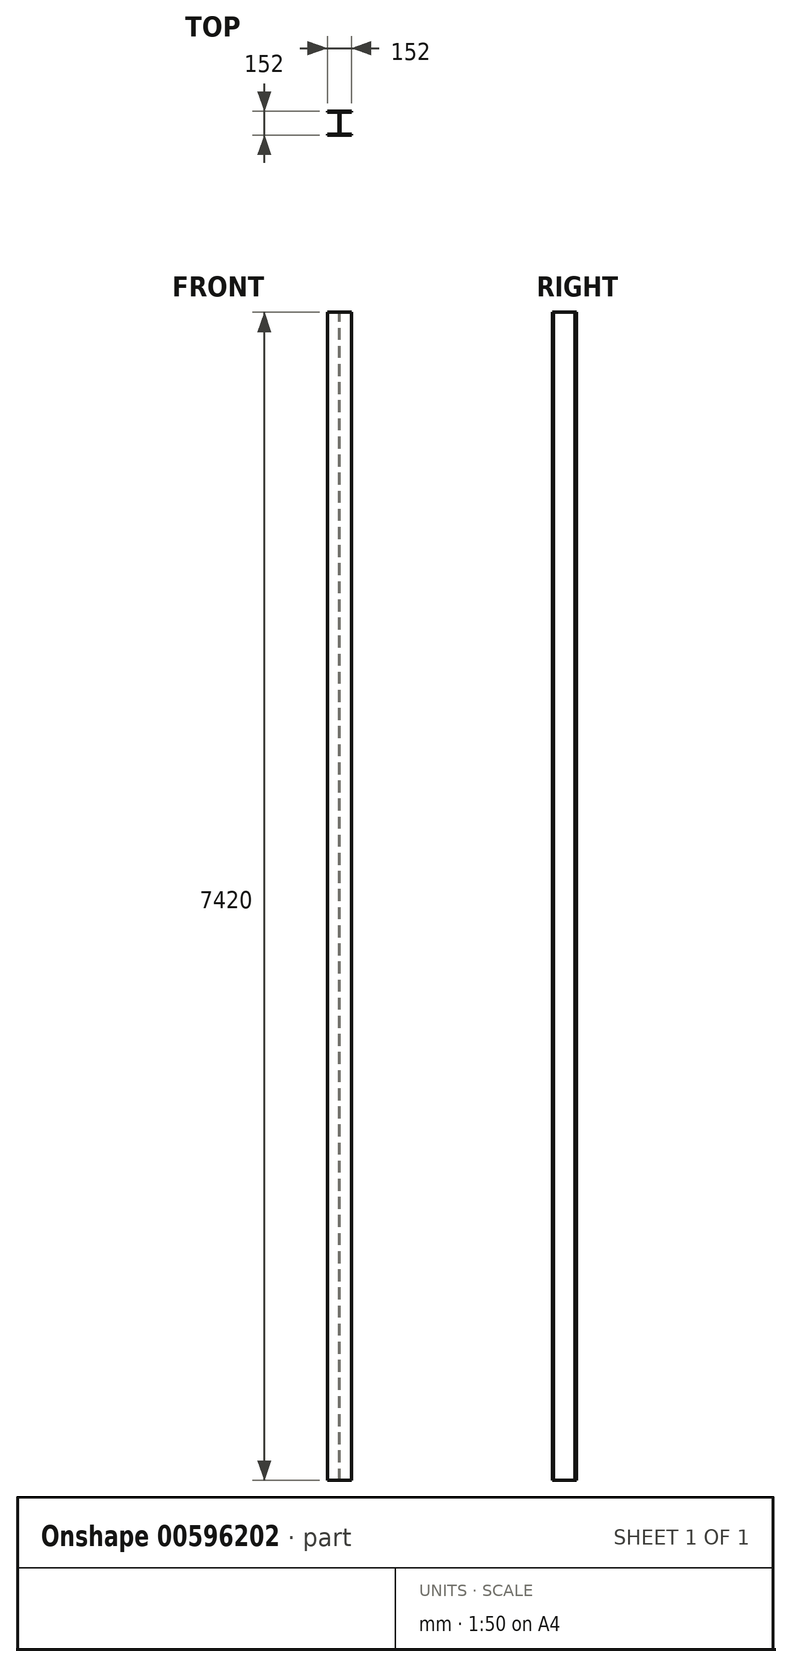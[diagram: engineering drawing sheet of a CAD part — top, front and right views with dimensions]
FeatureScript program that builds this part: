
annotation { "Feature Type Name" : "Feature", "Feature Type Description" : "" }
export const myFeature = defineFeature(function(context is Context, id is Id, definition is map)
    precondition{}
    {
        {
            var Q0;
            Q0=qCreatedBy(makeId("Top.planeOp"),FACE);
            var sketch = newSketch(context, id + "F0", { "sketchPlane" : qUnion([Q0])});
            skLineSegment(sketch, "E0.bottom", {"start": v(-132.33, 137.4) * mm, "end": v(19.67, 137.4) * mm, "construction": true});
            skLineSegment(sketch, "E0.top", {"start": v(-132.33, -14.6) * mm, "end": v(19.67, -14.6) * mm, "construction": true});
            skLineSegment(sketch, "E0.left", {"start": v(-132.33, 137.4) * mm, "end": v(-132.33, -14.6) * mm, "construction": true});
            skLineSegment(sketch, "E0.right", {"start": v(19.67, 137.4) * mm, "end": v(19.67, -14.6) * mm, "construction": true});
            skLineSegment(sketch, "E1", {"start": v(-59.38, 137.4) * mm, "end": v(-59.38, -14.6) * mm, "construction": true});
            skLineSegment(sketch, "E2", {"start": v(-53.28, 137.4) * mm, "end": v(-53.28, -14.6) * mm, "construction": true});
            skLineSegment(sketch, "E3", {"start": v(-132.33, 130.6) * mm, "end": v(19.67, 130.6) * mm, "construction": true});
            skLineSegment(sketch, "E4", {"start": v(-132.33, -7.8) * mm, "end": v(19.67, -7.8) * mm, "construction": true});
            skLineSegment(sketch, "E5", {"start": v(-132.33, 137.4) * mm, "end": v(-59.38, 137.4) * mm});
            skLineSegment(sketch, "E6", {"start": v(19.67, 137.4) * mm, "end": v(19.67, 130.6) * mm});
            skLineSegment(sketch, "E7", {"start": v(-132.33, 137.4) * mm, "end": v(19.67, 137.4) * mm});
            skLineSegment(sketch, "E8", {"start": v(19.67, 130.6) * mm, "end": v(-53.28, 130.6) * mm});
            skLineSegment(sketch, "E9", {"start": v(-53.28, 130.6) * mm, "end": v(-53.28, -7.8) * mm});
            skLineSegment(sketch, "E10", {"start": v(-53.28, -7.8) * mm, "end": v(19.67, -7.8) * mm});
            skLineSegment(sketch, "E11", {"start": v(19.67, -14.6) * mm, "end": v(-132.33, -14.6) * mm});
            skLineSegment(sketch, "E12", {"start": v(-132.33, -7.8) * mm, "end": v(-59.38, -7.8) * mm});
            skLineSegment(sketch, "E13", {"start": v(-59.38, -7.8) * mm, "end": v(-59.38, 130.6) * mm});
            skLineSegment(sketch, "E14", {"start": v(-59.38, 130.6) * mm, "end": v(-132.33, 130.6) * mm});
            skLineSegment(sketch, "E15", {"start": v(-132.33, 137.4) * mm, "end": v(-132.33, 130.6) * mm});
            skLineSegment(sketch, "E16", {"start": v(-132.33, -7.8) * mm, "end": v(-132.33, -14.6) * mm});
            skLineSegment(sketch, "E17", {"start": v(19.67, -7.8) * mm, "end": v(19.67, -14.6) * mm});
            skSolve(sketch);
        }
        {
            var Q0;
            {var subQ1=sQuery(id+"F0.wireOp",EDGE,"E6");Q0=makeQuery(id+"F0.imprint","IMPRINT",FACE,{"disambiguationData":[TD([[makeQuery(id+"F0.imprint","IMPRINT",EDGE,{"derivedFrom":subQ1}),-1.0]])]});}
            extrude(context, id + "F1", {"entities" : qUnion([Q0]), "oppositeDirection" : true, "depth" : 7420 * mm, "offsetDistance" : 25 * mm});
        }
    });
